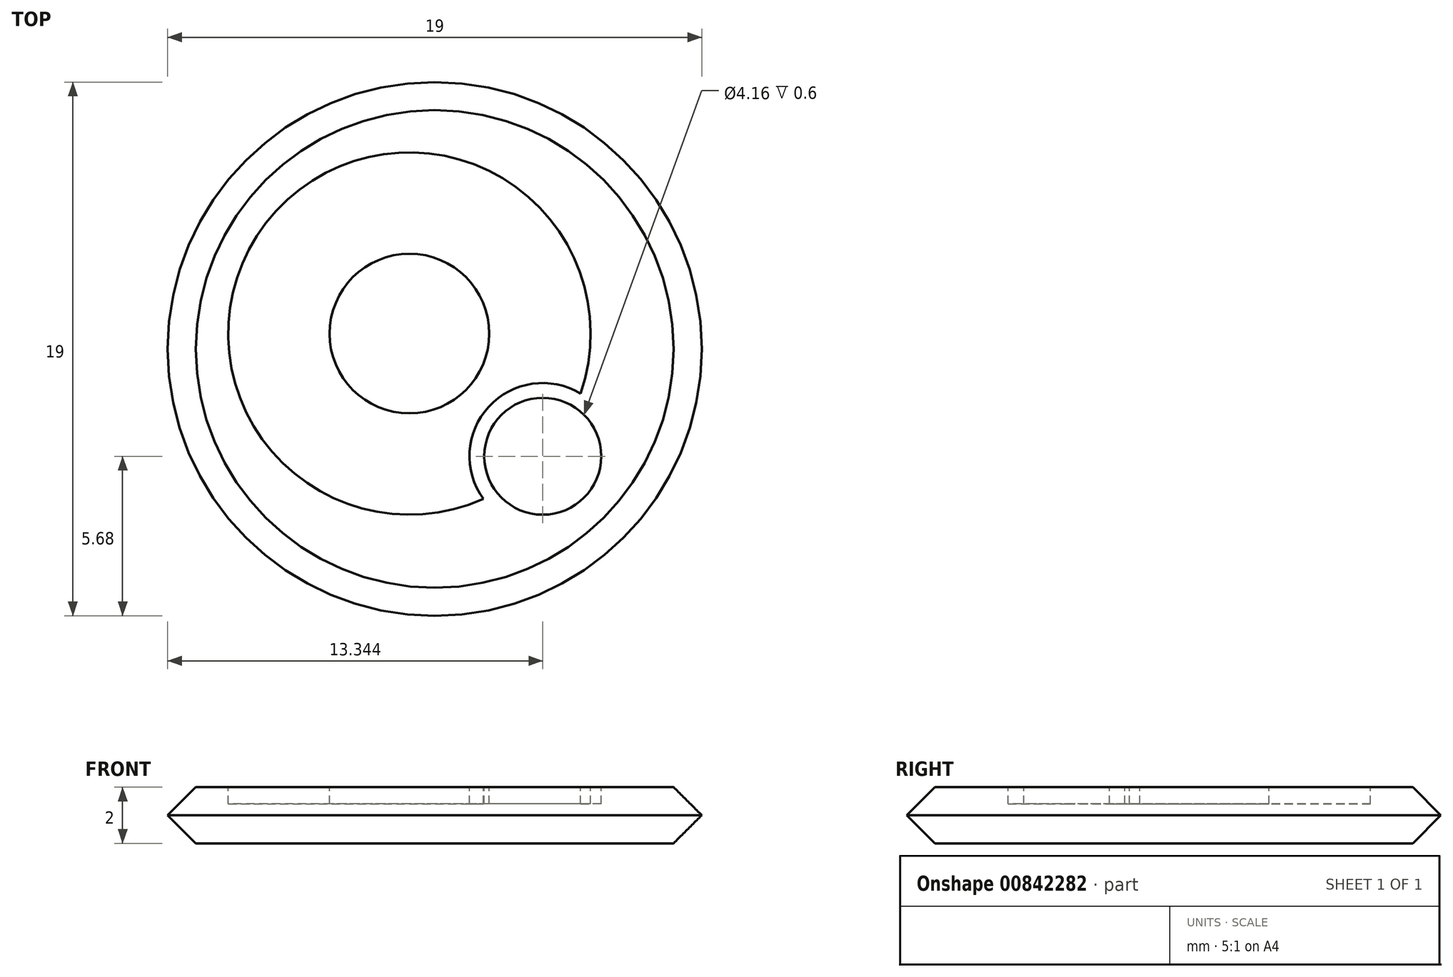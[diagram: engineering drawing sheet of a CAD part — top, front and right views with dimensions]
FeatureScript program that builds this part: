
annotation { "Feature Type Name" : "Feature", "Feature Type Description" : "" }
export const myFeature = defineFeature(function(context is Context, id is Id, definition is map)
    precondition{}
    {
        {
            var Q0;
            Q0=qCreatedBy(makeId("Top.planeOp"),FACE);
            var sketch = newSketch(context, id + "F0", { "sketchPlane" : qUnion([Q0])});
            skCircle(sketch, "E0", {"center": v(0, 0) * mm, "radius": 9.5 * mm});
            skSolve(sketch);
        }
        {
            var Q0;
            Q0=makeQuery(id+"F0.imprint","IMPRINT",FACE,{"disambiguationData":[TD([[makeQuery(id+"F0.imprint","IMPRINT",EDGE,{"derivedFrom":sQuery(id+"F0.wireOp",EDGE,"E0")}),1.0]])]});
            extrude(context, id + "F1", {"entities" : qUnion([Q0]), "depth" : 2 * mm, "offsetDistance" : 25 * mm});
        }
        {
            var Q0;
            Q0=makeQuery(id+"F1.opExtrude","CAP_EDGE",EDGE,{"disambiguationData":[OSD([sQuery(id+"F0.wireOp",EDGE,"E0")])],"isStart":false});
            var Q1;
            Q1=makeQuery(id+"F1.opExtrude","CAP_EDGE",EDGE,{"disambiguationData":[OSD([sQuery(id+"F0.wireOp",EDGE,"E0")])],"isStart":true});
            chamfer(context, id + "F2", {"entities" : qUnion([Q0, Q1]), "width" : 1 * mm, "tangentPropagation" : true});
        }
        {
            var Q0;
            Q0=makeQuery(id+"F1.opExtrude","CAP_FACE",FACE,{"disambiguationData":[OSD([sQuery(id+"F0.wireOp",EDGE,"E0")])],"isStart":false});
            var sketch = newSketch(context, id + "F3", { "sketchPlane" : qUnion([Q0])});
            skCircle(sketch, "E1", {"center": v(-0.9, 0.55) * mm, "radius": 6.45 * mm});
            skCircle(sketch, "E2", {"center": v(-0.9, 0.55) * mm, "radius": 2.84 * mm});
            skCircle(sketch, "E3", {"center": v(3.84, -3.82) * mm, "radius": 2.6 * mm});
            skCircle(sketch, "E4", {"center": v(3.84, -3.82) * mm, "radius": 2.08 * mm});
            skLineSegment(sketch, "E5", {"start": v(-0.9, -5.9) * mm, "end": v(3.84, -5.9) * mm, "construction": true});
            skSolve(sketch);
        }
        {
            var Q0;
            Q0=makeQuery(id+"F3.imprint","IMPRINT",FACE,{"disambiguationData":[TD([[makeQuery(id+"F3.imprint","IMPRINT",EDGE,{"derivedFrom":sQuery(id+"F3.wireOp",EDGE,"E2")}),-1.0]])]});
            var Q1;
            {var subQ0=sQuery(id+"F3.wireOp",EDGE,"E4");var subQ1=sQuery(id+"F3.wireOp",EDGE,"E1");var subQ2=makeQuery(id+"F3.imprint","INTERSECT",VERTEX,{"disambiguationData":[OD(0.0)],"derivedFrom":[subQ1,subQ0]});Q1=makeQuery(id+"F3.imprint","IMPRINT",FACE,{"disambiguationData":[TD([[makeQuery(id+"F3.imprint","IMPRINT",EDGE,{"disambiguationData":[TD([[subQ2,-1.0]])],"derivedFrom":subQ1}),1.0]])]});}
            var Q2;
            {var subQ0=sQuery(id+"F3.wireOp",EDGE,"E4");var subQ1=sQuery(id+"F3.wireOp",EDGE,"E1");var subQ2=makeQuery(id+"F3.imprint","INTERSECT",VERTEX,{"disambiguationData":[OD(0.0)],"derivedFrom":[subQ1,subQ0]});Q2=makeQuery(id+"F3.imprint","IMPRINT",FACE,{"disambiguationData":[TD([[makeQuery(id+"F3.imprint","IMPRINT",EDGE,{"disambiguationData":[TD([[subQ2,-1.0]])],"derivedFrom":subQ1}),-1.0]])]});}
            extrude(context, id + "F4", {"entities" : qUnion([Q0, Q1, Q2]), "operationType" : NewBodyOperationType.REMOVE, "oppositeDirection" : true, "depth" : 0.6 * mm, "offsetDistance" : 25 * mm});
        }
    });
